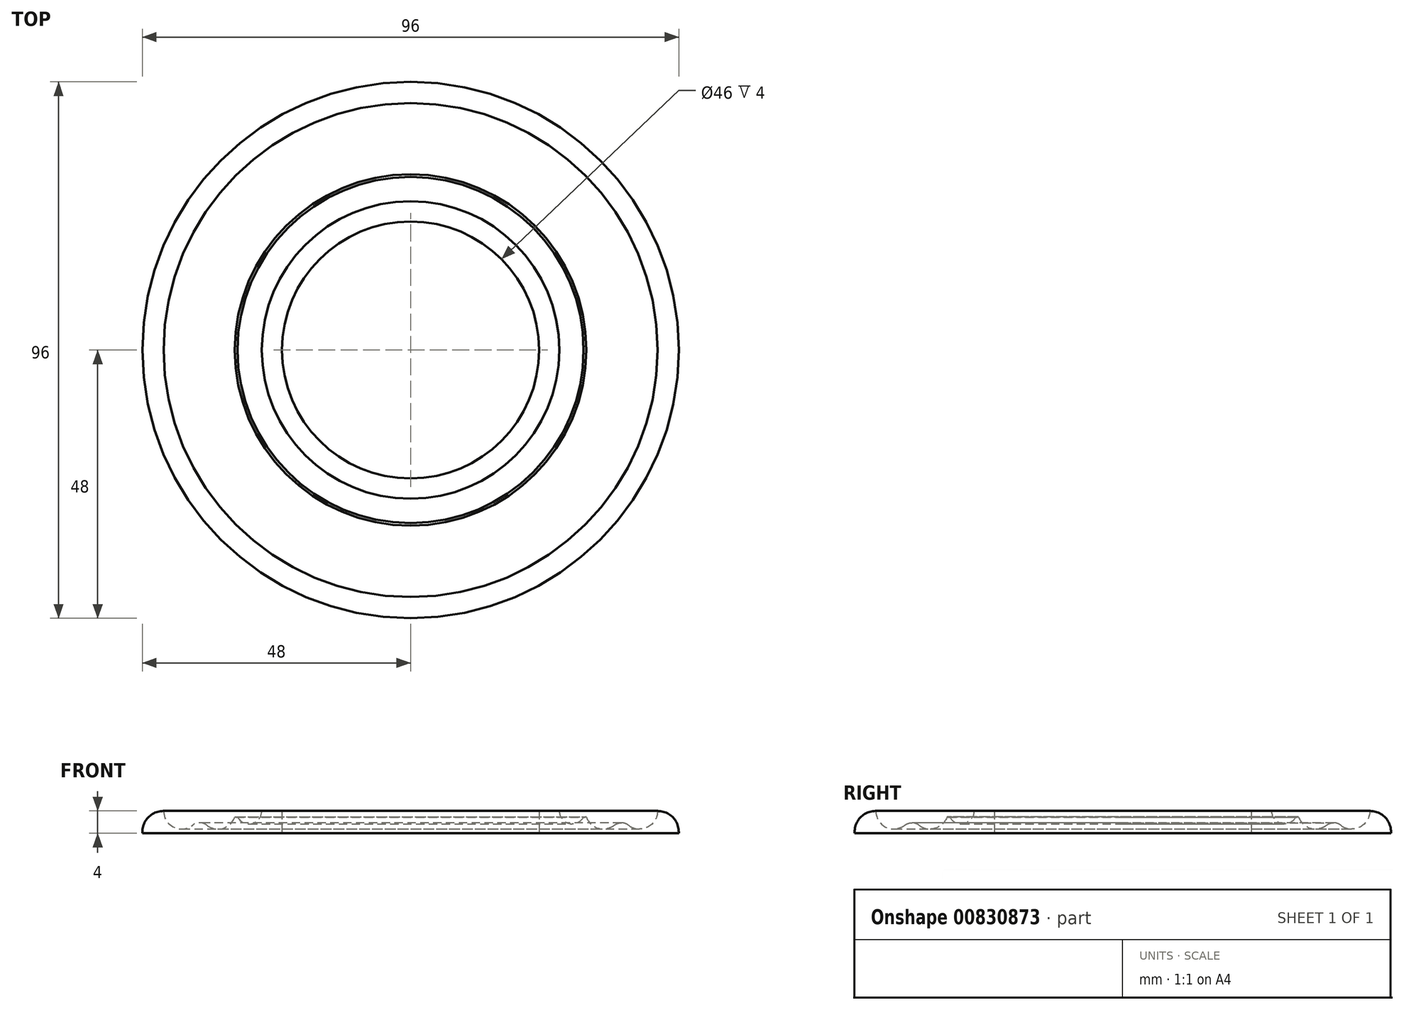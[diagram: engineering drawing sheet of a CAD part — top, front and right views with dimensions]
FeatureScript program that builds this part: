
annotation { "Feature Type Name" : "Feature", "Feature Type Description" : "" }
export const myFeature = defineFeature(function(context is Context, id is Id, definition is map)
    precondition{}
    {
        {
            var Q0;
            Q0=qCreatedBy(makeId("Front.planeOp"),FACE);
            var sketch = newSketch(context, id + "F0", { "sketchPlane" : qUnion([Q0])});
            skLineSegment(sketch, "E0", {"start": v(-23, 0) * mm, "end": v(-48, 0) * mm});
            skLineSegment(sketch, "E1", {"start": v(-48, 0) * mm, "end": v(-48, 0.24) * mm});
            skLineSegment(sketch, "E2", {"start": v(-23, 0) * mm, "end": v(-23, 4) * mm});
            skLineSegment(sketch, "E3", {"start": v(-23, 4) * mm, "end": v(-26.62, 4) * mm});
            skLineSegment(sketch, "E4", {"start": v(0, 0) * mm, "end": v(0, 4) * mm});
            skPoint(sketch, "E5.visualSharp", {"position": v(-48, 4) * mm});
            skArc(sketch, "E5.filletArc", {"start": v(-44.24, 4) * mm, "mid": v(-46.9, 2.9) * mm, "end": v(-48, 0.24) * mm});
            skArc(sketch, "E6", {"start": v(-44.2, 4) * mm, "mid": v(-42.38, 1.1) * mm, "end": v(-38.97, 1.46) * mm});
            skLineSegment(sketch, "E7.trimOffspring", {"start": v(-44.2, 4) * mm, "end": v(-44.24, 4) * mm});
            skArc(sketch, "E8", {"start": v(-36.5, 1.46) * mm, "mid": v(-33.6, 0.9) * mm, "end": v(-31.45, 2.93) * mm});
            skPoint(sketch, "E9.visualSharp", {"position": v(-37.73, 4) * mm});
            skArc(sketch, "E9.filletArc", {"start": v(-36.5, 1.46) * mm, "mid": v(-37.73, 1.88) * mm, "end": v(-38.97, 1.46) * mm});
            skArc(sketch, "E10", {"start": v(-30.98, 2.94) * mm, "mid": v(-28.38, 1.76) * mm, "end": v(-26.62, 4) * mm});
            skLineSegment(sketch, "E11.trimOffspring", {"start": v(-31.23, 4) * mm, "end": v(-31.27, 4) * mm});
            skArc(sketch, "E12", {"start": v(-31.45, 2.93) * mm, "mid": v(-31.21, 2.9) * mm, "end": v(-30.98, 2.94) * mm});
            skSolve(sketch);
        }
        {
            var Q0;
            Q0=makeQuery(id+"F0.imprint","IMPRINT",FACE,{"disambiguationData":[TD([[makeQuery(id+"F0.imprint","IMPRINT",EDGE,{"derivedFrom":sQuery(id+"F0.wireOp",EDGE,"E0")}),-1.0]])]});
            var Q1;
            Q1=sQuery(id+"F0.wireOp",EDGE,"E4");
            revolve(context, id + "F1", {"surfaceOperationType" : NewSurfaceOperationType.NEW, "entities" : qUnion([Q0]), "axis" : qUnion([Q1]), "revolveType" : RevolveType.FULL});
        }
    });
